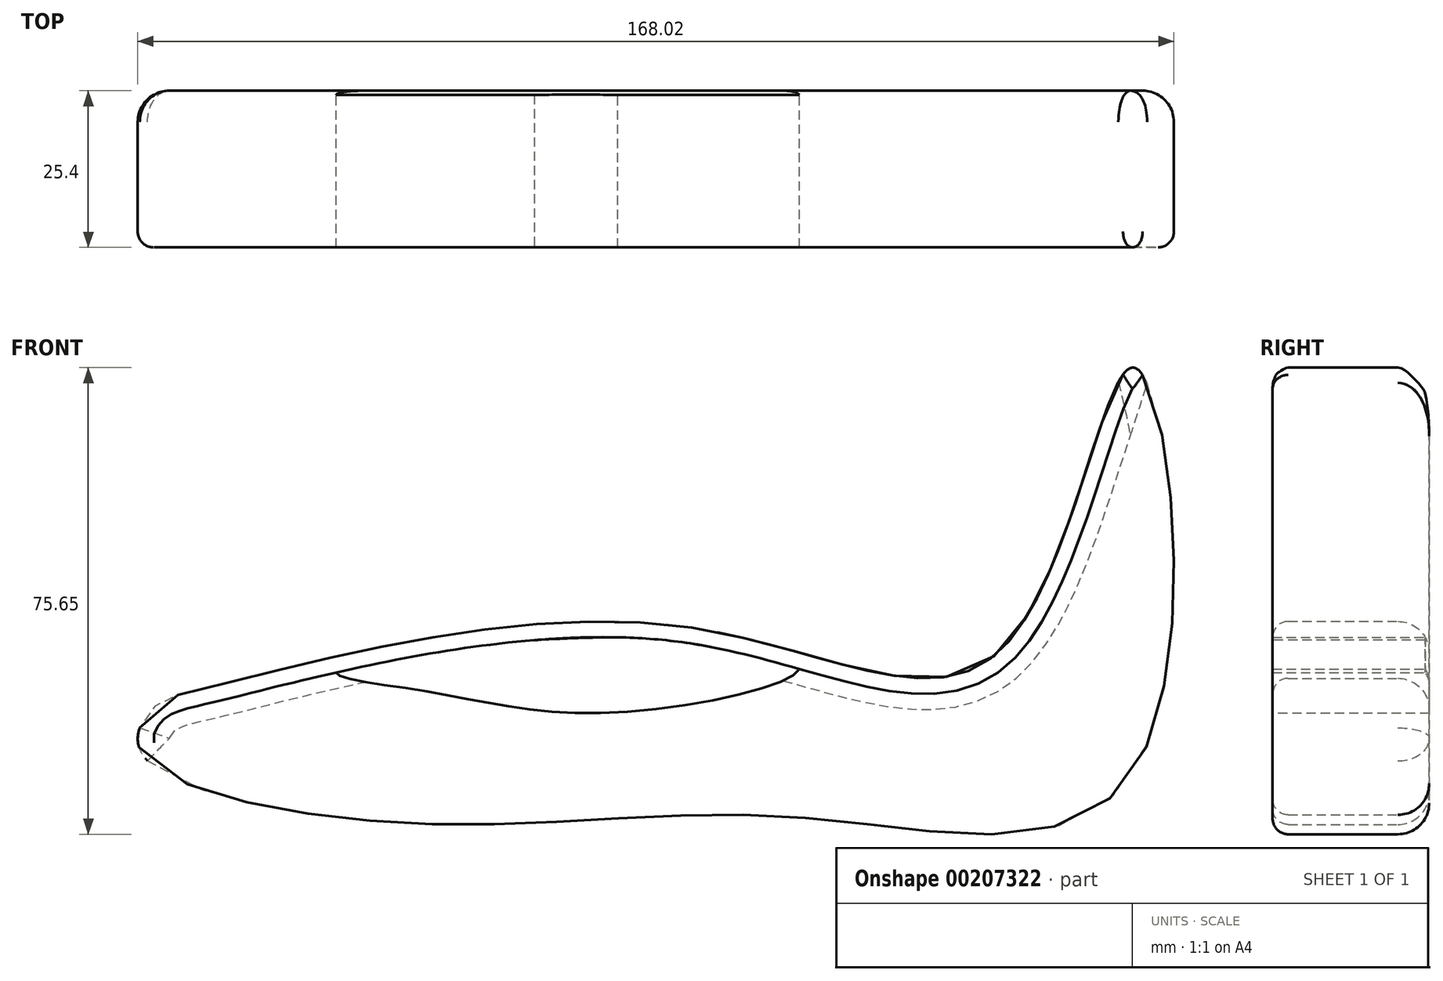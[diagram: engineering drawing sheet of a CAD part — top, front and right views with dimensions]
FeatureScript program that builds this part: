
annotation { "Feature Type Name" : "Feature", "Feature Type Description" : "" }
export const myFeature = defineFeature(function(context is Context, id is Id, definition is map)
    precondition{}
    {
        {
            var Q0;
            Q0=qCreatedBy(makeId("Front.planeOp"),FACE);
            var sketch = newSketch(context, id + "F0", { "sketchPlane" : qUnion([Q0])});
            skFitSpline(sketch, "E0", {"points": [v(-51.34, 18.11) * mm, v(-61.33, 14.4) * mm, v(-63.04, 7.27) * mm, v(-19.4, -4.14) * mm, v(45.07, -3.28) * mm, v(98.4, 5.28) * mm, v(97.84, 69.74) * mm, v(76.73, 24.39) * mm, v(24.53, 27.81) * mm, v(-51.34, 18.11) * mm]});
            skSolve(sketch);
        }
        {
            var Q0;
            Q0=makeQuery(id+"F0.imprint","IMPRINT",FACE,{"disambiguationData":[TD([[makeQuery(id+"F0.imprint","IMPRINT",EDGE,{"derivedFrom":sQuery(id+"F0.wireOp",EDGE,"E0")}),1.0]])]});
            var Q1;
            Q1=sQuery(id+"F0.wireOp",EDGE,"E0");
            extrude(context, id + "F1", {"entities" : qUnion([Q0]), "surfaceEntities" : qUnion([Q1]), "depth" : 25.4 * mm});
        }
        {
            var Q0;
            Q0=makeQuery(id+"F1.opExtrude","CAP_FACE",FACE,{"disambiguationData":[OSD([sQuery(id+"F0.wireOp",EDGE,"E0")])],"isStart":false});
            fillet(context, id + "F2", {"entities" : qUnion([Q0]), "radius" : 2.54 * mm, "tangentPropagation" : true, "allowEdgeOverflow" : false});
        }
        {
            var Q0;
            Q0=makeQuery(id+"F1.opExtrude","SWEPT_FACE",FACE,{"disambiguationData":[OSD([sQuery(id+"F0.wireOp",EDGE,"E0")])]});
            fillet(context, id + "F3", {"entities" : qUnion([Q0]), "radius" : 5.08 * mm, "tangentPropagation" : true, "allowEdgeOverflow" : false});
        }
        {
            var Q0;
            Q0=makeQuery(id+"F1.opExtrude","CAP_FACE",FACE,{"disambiguationData":[OSD([sQuery(id+"F0.wireOp",EDGE,"E0")])],"isStart":false});
            var sketch = newSketch(context, id + "F4", { "sketchPlane" : qUnion([Q0])});
            skFitSpline(sketch, "E1", {"points": [v(-31.46, 20.33) * mm, v(-17.1, 17.3) * mm, v(12.88, 13.78) * mm, v(43.63, 20.9) * mm, v(14.2, 26.02) * mm, v(-31.46, 20.33) * mm]});
            skSolve(sketch);
        }
        {
            var Q0;
            {var subQ0=sQuery(id+"F4.wireOp",EDGE,"E1");var subQ1=sQuery(id+"F0.wireOp",EDGE,"E0");var subQ2=makeQuery(id+"F2.opFillet","BLEND_EDGE",EDGE,{"disambiguationData":[OD(0.0)],"blendedFrom":[makeQuery(id+"F1.opExtrude","CAP_EDGE",EDGE,{"disambiguationData":[OSD([subQ1])],"isStart":false}),makeQuery(id+"F1.opExtrude","CAP_FACE",FACE,{"disambiguationData":[OSD([subQ1])],"isStart":false})],"blendedInto":[makeQuery(id+"F1.opExtrude","CAP_FACE",FACE,{"disambiguationData":[OSD([subQ1])],"isStart":false})]});var subQ3=makeQuery(id+"F4.imprint","INTERSECT",VERTEX,{"disambiguationData":[OD(0.0)],"derivedFrom":[subQ2,subQ0]});Q0=makeQuery(id+"F4.imprint","IMPRINT",FACE,{"disambiguationData":[TD([[makeQuery(id+"F4.imprint","IMPRINT",EDGE,{"disambiguationData":[TD([[subQ3,-1.0]])],"derivedFrom":subQ0}),1.0]])]});}
            var Q1;
            Q1=sQuery(id+"F4.wireOp",EDGE,"E1");
            extrude(context, id + "F5", {"entities" : qUnion([Q0]), "operationType" : NewBodyOperationType.REMOVE, "surfaceEntities" : qUnion([Q1]), "oppositeDirection" : true, "depth" : 25.4 * mm});
        }
    });
